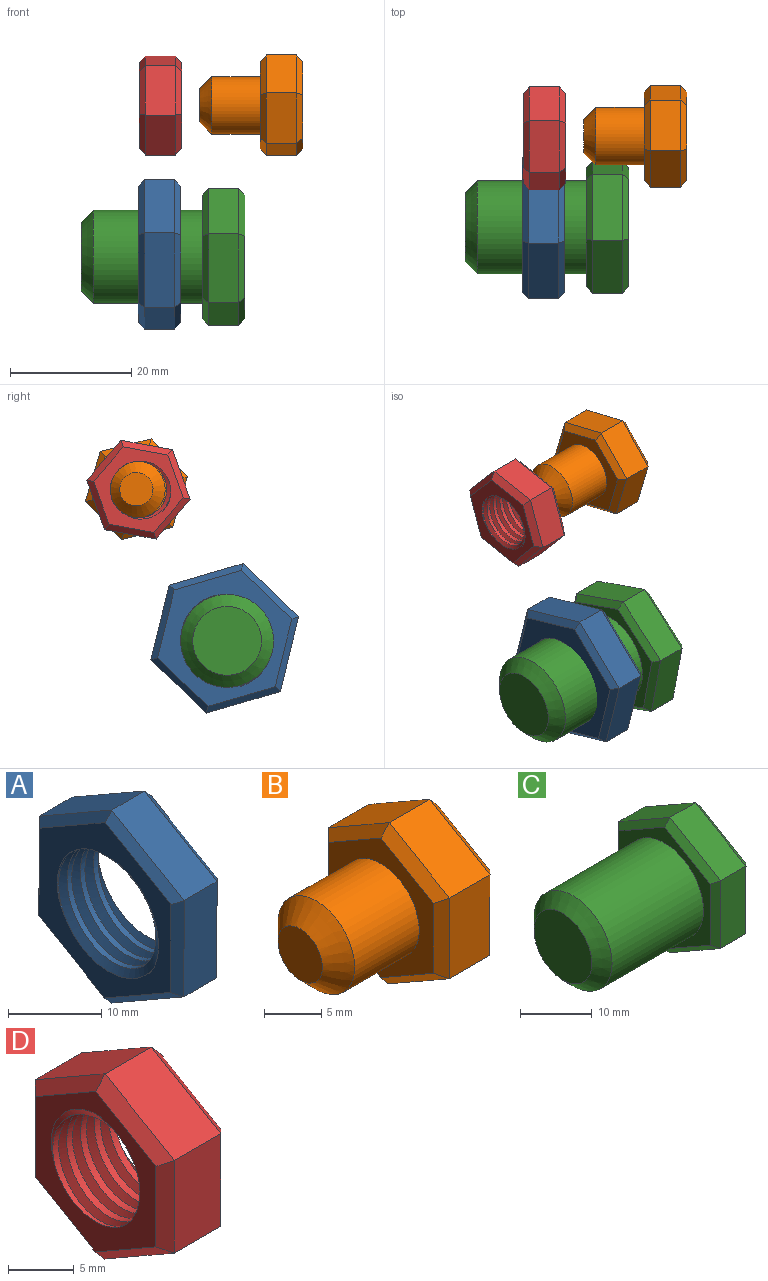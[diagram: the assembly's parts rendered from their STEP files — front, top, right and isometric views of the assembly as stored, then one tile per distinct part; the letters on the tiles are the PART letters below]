
ASSEMBLY  parts=4 mates=2
PART A: 23 faces, bbox 9.3x22.7x26 mm
  f0: cylinder r=7.24mm len=14.48mm, axis (1,0,0), area 111.6mm2, adj f7,f8,f21,f22
  f1: plane 10.98x6.38mm, normal (0,-0.5,0.86), area 63.5mm2, adj f2,f6,f14,f18
  f2: plane 12.7x5mm, normal (0,-1,0), area 63.5mm2, adj f1,f3,f12,f16
  f3: plane 11.02x6.32mm, normal (0,-0.5,-0.87), area 63.5mm2, adj f2,f4,f10,f15
  f4: plane 10.98x6.38mm, normal (0,0.5,-0.86), area 63.5mm2, adj f3,f5,f9,f17
  f5: plane 12.7x5mm, normal (0,1,0), area 63.5mm2, adj f4,f6,f11,f19
  f6: plane 11.02x6.32mm, normal (0,0.5,0.87), area 63.5mm2, adj f1,f5,f13,f20
  f7: plane 23.73x20.67mm, normal (-1,0,0), area 164.4mm2, adj f0,f9,f10,f11,f12,f13,f14,f21
  f8: plane 23.73x20.67mm, normal (1,0,0), area 164.4mm2, adj f0,f15,f16,f17,f18,f19,f20,f21
  f9: plane 10.99x6.96mm, normal (-0.71,0.36,-0.61), area 17.1mm2, adj f4,f7,f10,f11
  f10: plane 11.02x6.9mm, normal (-0.71,-0.35,-0.61), area 17.1mm2, adj f3,f7,f9,f12
  f11: plane 12.7x1.03mm, normal (-0.71,0.71,0), area 17.1mm2, adj f5,f7,f9,f13
  f12: plane 12.7x1.03mm, normal (-0.71,-0.71,0), area 17.1mm2, adj f2,f7,f10,f14
  f13: plane 11.02x6.9mm, normal (-0.71,0.35,0.61), area 17.1mm2, adj f6,f7,f11,f14
  f14: plane 10.99x6.96mm, normal (-0.71,-0.36,0.61), area 17.1mm2, adj f1,f7,f12,f13
  f15: plane 11.02x6.9mm, normal (0.71,-0.35,-0.61), area 17.1mm2, adj f3,f8,f16,f17
  f16: plane 12.7x1.03mm, normal (0.71,-0.71,0), area 17.1mm2, adj f2,f8,f15,f18
  f17: plane 10.99x6.96mm, normal (0.71,0.36,-0.61), area 17.1mm2, adj f4,f8,f15,f19
  f18: plane 10.99x6.96mm, normal (0.71,-0.36,0.61), area 17.1mm2, adj f1,f8,f16,f20
  f19: plane 12.7x1.03mm, normal (0.71,0.71,0), area 17.1mm2, adj f5,f8,f17,f20
  f20: plane 11.02x6.9mm, normal (0.71,0.35,0.61), area 17.1mm2, adj f6,f8,f18,f19
  f21: bspline ~19.31x16.73mm, area 223mm2, adj f0,f7,f8,f22
  f22: bspline ~19.31x16.73mm, area 223mm2, adj f0,f7,f8,f21
PART B: 23 faces, bbox 17x15x17.3 mm
  f0: cylinder r=4.75mm len=9.5mm, axis (1,0,0), area 238.8mm2, adj f2,f10
  f1: plane 5.5x5.5mm, normal (-1,0,0), area 23.8mm2, adj f2
  f2: cone r=4.75mm half-angle=45deg, axis (1,0,0), area 66.6mm2, adj f0,f1
  f3: plane 7.48x5mm, normal (0,-0.5,0.86), area 43.3mm2, adj f4,f8,f16,f20
  f4: plane 8.66x5mm, normal (0,-1,0), area 43.3mm2, adj f3,f5,f14,f18
  f5: plane 7.52x5mm, normal (0,-0.5,-0.87), area 43.3mm2, adj f4,f6,f12,f17
  f6: plane 7.48x5mm, normal (0,0.5,-0.86), area 43.3mm2, adj f5,f7,f11,f19
  f7: plane 8.66x5mm, normal (0,1,0), area 43.3mm2, adj f6,f8,f13,f21
  f8: plane 7.52x5mm, normal (0,0.5,0.87), area 43.3mm2, adj f3,f7,f15,f22
  f9: plane 15.01x13.03mm, normal (1,0,0), area 146.4mm2, adj f11,f12,f13,f14,f15,f16
  f10: plane 15.01x13.03mm, normal (-1,0,0), area 75.5mm2, adj f0,f17,f18,f19,f20,f21,f22
  f11: plane 7.49x4.93mm, normal (0.71,0.36,-0.61), area 11.4mm2, adj f6,f9,f12,f13
  f12: plane 7.52x4.88mm, normal (0.71,-0.35,-0.61), area 11.4mm2, adj f5,f9,f11,f14
  f13: plane 8.66x1.03mm, normal (0.71,0.71,0), area 11.4mm2, adj f7,f9,f11,f15
  f14: plane 8.66x1.03mm, normal (0.71,-0.71,0), area 11.4mm2, adj f4,f9,f12,f16
  f15: plane 7.52x4.88mm, normal (0.71,0.35,0.61), area 11.4mm2, adj f8,f9,f13,f16
  f16: plane 7.49x4.93mm, normal (0.71,-0.36,0.61), area 11.4mm2, adj f3,f9,f14,f15
  f17: plane 7.52x4.88mm, normal (-0.71,-0.35,-0.61), area 11.4mm2, adj f5,f10,f18,f19
  f18: plane 8.66x1.03mm, normal (-0.71,-0.71,0), area 11.4mm2, adj f4,f10,f17,f20
  f19: plane 7.49x4.93mm, normal (-0.71,0.36,-0.61), area 11.4mm2, adj f6,f10,f17,f21
  f20: plane 7.49x4.93mm, normal (-0.71,-0.36,0.61), area 11.4mm2, adj f3,f10,f18,f22
  f21: plane 8.66x1.03mm, normal (-0.71,0.71,0), area 11.4mm2, adj f7,f10,f19,f22
  f22: plane 7.52x4.88mm, normal (-0.71,0.35,0.61), area 11.4mm2, adj f8,f10,f20,f21
PART C: 23 faces, bbox 27x20x23.1 mm
  f0: cylinder r=7.68mm len=18mm, axis (1,0,0), area 868.6mm2, adj f2,f10
  f1: plane 11.36x11.36mm, normal (-1,0,0), area 101.4mm2, adj f2
  f2: cone r=7.68mm half-angle=45deg, axis (1,0,0), area 118.7mm2, adj f0,f1
  f3: plane 9.98x5.81mm, normal (0,-0.5,0.86), area 57.7mm2, adj f4,f8,f16,f20
  f4: plane 11.55x5mm, normal (0,-1,0), area 57.7mm2, adj f3,f5,f14,f18
  f5: plane 10.02x5.74mm, normal (0,-0.5,-0.87), area 57.7mm2, adj f4,f6,f12,f17
  f6: plane 9.98x5.81mm, normal (0,0.5,-0.86), area 57.7mm2, adj f5,f7,f11,f19
  f7: plane 11.55x5mm, normal (0,1,0), area 57.7mm2, adj f6,f8,f13,f21
  f8: plane 10.02x5.74mm, normal (0,0.5,0.87), area 57.7mm2, adj f3,f7,f15,f22
  f9: plane 20.78x18.04mm, normal (1,0,0), area 280.6mm2, adj f11,f12,f13,f14,f15,f16
  f10: plane 20.78x18.04mm, normal (-1,0,0), area 95.3mm2, adj f0,f17,f18,f19,f20,f21,f22
  f11: plane 9.98x6.38mm, normal (0.71,0.36,-0.61), area 15.5mm2, adj f6,f9,f12,f13
  f12: plane 10.02x6.32mm, normal (0.71,-0.35,-0.61), area 15.5mm2, adj f5,f9,f11,f14
  f13: plane 11.55x1.04mm, normal (0.71,0.71,0), area 15.5mm2, adj f7,f9,f11,f15
  f14: plane 11.55x1.04mm, normal (0.71,-0.71,0), area 15.5mm2, adj f4,f9,f12,f16
  f15: plane 10.02x6.32mm, normal (0.71,0.35,0.61), area 15.5mm2, adj f8,f9,f13,f16
  f16: plane 9.98x6.38mm, normal (0.71,-0.36,0.61), area 15.5mm2, adj f3,f9,f14,f15
  f17: plane 10.02x6.32mm, normal (-0.71,-0.35,-0.61), area 15.5mm2, adj f5,f10,f18,f19
  f18: plane 11.55x1.04mm, normal (-0.71,-0.71,0), area 15.5mm2, adj f4,f10,f17,f20
  f19: plane 9.98x6.38mm, normal (-0.71,0.36,-0.61), area 15.5mm2, adj f6,f10,f17,f21
  f20: plane 9.98x6.38mm, normal (-0.71,-0.36,0.61), area 15.5mm2, adj f3,f10,f18,f22
  f21: plane 11.55x1.04mm, normal (-0.71,0.71,0), area 15.5mm2, adj f7,f10,f19,f22
  f22: plane 10.02x6.32mm, normal (-0.71,0.35,0.61), area 15.5mm2, adj f8,f10,f20,f21
PART D: 23 faces, bbox 9.1x15.4x17.7 mm
  f0: plane 7.51x5mm, normal (0,0.5,0.87), area 43.3mm2, adj f1,f5,f12,f19
  f1: plane 7.49x5mm, normal (0,-0.5,0.86), area 43.3mm2, adj f0,f2,f13,f17
  f2: plane 8.66x5mm, normal (0,-1,0), area 43.3mm2, adj f1,f3,f11,f15
  f3: plane 7.51x5mm, normal (0,-0.5,-0.87), area 43.3mm2, adj f2,f4,f9,f14
  f4: plane 7.49x5mm, normal (0,0.5,-0.86), area 43.3mm2, adj f3,f5,f8,f16
  f5: plane 8.66x5mm, normal (0,1,0), area 43.3mm2, adj f0,f4,f10,f18
  f6: plane 15.37x13.38mm, normal (-1,0,0), area 71.4mm2, adj f8,f9,f10,f11,f12,f13,f20,f21
  f7: plane 15.37x13.38mm, normal (1,0,0), area 71.4mm2, adj f14,f15,f16,f17,f18,f19,f20,f21
  f8: plane 7.49x4.93mm, normal (-0.71,0.36,-0.61), area 11.4mm2, adj f4,f6,f9,f10
  f9: plane 7.51x4.89mm, normal (-0.71,-0.35,-0.61), area 11.4mm2, adj f3,f6,f8,f11
  f10: plane 8.66x1.02mm, normal (-0.71,0.71,0), area 11.4mm2, adj f5,f6,f8,f12
  f11: plane 8.66x1.02mm, normal (-0.71,-0.71,0), area 11.4mm2, adj f2,f6,f9,f13
  f12: plane 7.51x4.89mm, normal (-0.71,0.35,0.61), area 11.4mm2, adj f0,f6,f10,f13
  f13: plane 7.49x4.93mm, normal (-0.71,-0.36,0.61), area 11.4mm2, adj f1,f6,f11,f12
  f14: plane 7.51x4.89mm, normal (0.71,-0.35,-0.61), area 11.4mm2, adj f3,f7,f15,f16
  f15: plane 8.66x1.02mm, normal (0.71,-0.71,0), area 11.4mm2, adj f2,f7,f14,f17
  f16: plane 7.49x4.93mm, normal (0.71,0.36,-0.61), area 11.4mm2, adj f4,f7,f14,f18
  f17: plane 7.49x4.93mm, normal (0.71,-0.36,0.61), area 11.4mm2, adj f1,f7,f15,f19
  f18: plane 8.66x1.02mm, normal (0.71,0.71,0), area 11.4mm2, adj f5,f7,f16,f19
  f19: plane 7.51x4.89mm, normal (0.71,0.35,0.61), area 11.4mm2, adj f0,f7,f17,f18
  f20: cylinder r=4.66mm len=9.32mm, axis (1,0,0), area 85.4mm2, adj f6,f7,f21,f22
  f21: bspline ~12.5x10.82mm, area 128.5mm2, adj f6,f7,f20,f22
  f22: bspline ~12.5x10.82mm, area 128.4mm2, adj f6,f7,f20,f21
PLACE A rot(axis=(0,0.6,-0.8),180deg) t=(-55.27,-6.86,23.48)mm fixed
PLACE B rot(axis=(-1,0,0),43.8deg) t=(-31.66,7.73,48.08)mm
PLACE C rot(axis=(1,0,0),130.6deg) t=(-41.2,-7.25,23.06)mm
PLACE D rot(axis=(1,0,0),100.2deg) t=(-48.16,7.38,48.02)mm fixed
MATE cylindrical C.f0 <-> A.f7  axis (-1,0,0) through (-64.7,-7.25,23.06)mm
MATE cylindrical B.f0 <-> D.f6  axis (-1,0,0) through (-45.16,7.73,48.08)mm
